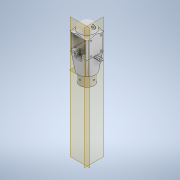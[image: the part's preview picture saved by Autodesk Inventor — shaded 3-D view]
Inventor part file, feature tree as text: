
AUTODESK INVENTOR PART (.ipt)
format: ipt  version: 2022.3 (Build 263350000, 350)  size: 754,688 bytes
history: native  units: mm
features: sketch x23, extrude x15, thicken_offset x6, fillet x5, hole x5, plane x4, revolve x2, mirror x2, projected_geometry x2, loft x1, sweep x1, other x1
ambient origin geometry x8: Origin, YZ Plane, XZ Plane, XY Plane, X Axis, Y Axis, Z Axis, Center Point
bodies: Solid1 (feature_tree)
feature tree (67):
  extrude  "Extrusion1"  Depth=4.0mm
  revolve  "Revolution1"  [1 undecoded]
  plane  "Work Plane1"
  extrude  "Extrusion2"  Depth=100.0mm
  extrude  "Extrusion3"  Depth=150.0mm
  plane  "Work Plane2"
  sketch  "Sketch5"  dims[d12=100.0mm d13=90.0deg]
  fillet  "Fillet1"  Radius=4.0mm
  loft  "Loft1"
  extrude  "Extrusion4"  Depth=5.0mm
  sketch  "Sketch11"  dims[d16=65.0mm d17=65.0mm]
  extrude  "Extrusion7"  Depth=65.0mm
  extrude  "Extrusion8"  Depth=15.0mm
  extrude  "Extrusion9"  Depth=5.0mm TaperAngle=0.0deg
  hole  "Hole2"  [1 undecoded]
  extrude  "Extrusion10"  Depth=50.0mm
  revolve  "Revolution2"  Angle=90.0deg
  fillet  "Fillet3"  [1 undecoded]
  hole  "Hole3"  [1 undecoded]
  hole  "Hole4"  [1 undecoded]
  extrude  "Extrusion14"  Depth=45.0mm
  sketch  "Sketch22"  dims[d58=45.0mm d59=0.0mm d60=45.0mm]
  extrude  "Extrusion15"  Depth=42.0mm TaperAngle=0.0deg
  extrude  "Extrusion16"  Depth=31.0mm
  plane  "Work Plane3"
  plane  "Work Plane4"
  sketch  "Sketch23"  dims[d61=22.0mm d62=42.0mm d63=0.0mm]
  sketch  "Sketch24"  dims[d64=31.0mm d65=31.0mm]
  hole  "Hole5"  [1 undecoded]
  hole  "Hole6"  [1 undecoded]
  mirror  "Mirror1"
  mirror  "Mirror2"
  thicken_offset  "Thicken1"
  thicken_offset  "Thicken2"
  thicken_offset  "Thicken3"
  thicken_offset  "Thicken4"
  thicken_offset  "Thicken5"
  extrude  "Extrusion17"  Depth=10.0mm
  fillet  "Fillet4"  [1 undecoded]
  extrude  "Extrusion18"  Depth=5.0mm
  extrude  "Extrusion19"  Depth=5.068mm
  fillet  "Fillet5"  Radius=5.0mm
  sweep  "Sweep1"
  thicken_offset  "Thicken6"
  extrude  "Extrusion20"  Depth=5.0mm
  fillet  "Fillet6"  Radius=5.068mm
  sketch  "Sketch1"  dims[d0=80.0mm d1=4.0mm]
  sketch  "Sketch2"  dims[d2=40.0mm d3=0.0mm d4=88.0mm]
  sketch  "Sketch3"  dims[d5=50.0mm d8=100.0mm]
  sketch  "Sketch4"  dims[d9=25.0mm d10=150.0mm d11=4.0mm]
  other  "Edges1"
  sketch  "Sketch7"  dims[d14=-52.5mm d15=5.0mm]
  projected_geometry  "Projected Loop2"
  sketch  "Sketch12"  dims[d18=5.0mm d19=15.0mm]
  sketch  "Sketch13"  dims[d20=10.0mm d21=5.0mm d22=0.0mm]
  sketch  "Sketch14"  dims[d23=52.0mm d24=52.0mm]
  sketch  "Sketch15"  dims[d25=5.0mm d26=0.0mm d27=50.0mm]
  sketch  "Sketch16"  dims[d28=5.0mm d29=0.0mm d30=90.0deg d31=0.0mm d32=90.0deg]
  sketch  "Sketch17"  dims[d33=100.0mm d34=0.0mm d54=5.0mm]
  sketch  "Sketch21"  dims[d55=4.5mm d56=5.0mm d57=0.0mm]
  sketch  "Sketch25"  dims[d66=3.4mm d67=6.0mm d68=5.9mm d69=2.0mm d70=90.0deg d71=5.0mm d72=0.0mm d73=3.0mm d74=0.0mm]
  sketch  "Sketch26"  dims[d75=26.0mm d76=26.0mm]
  sketch  "Sketch27"  dims[d77=90.0deg d78=10.0mm d79=0.0mm]
  projected_geometry  "Projected Loop3"
  sketch  "Sketch28"  dims[d80=5.0mm d81=5.0mm]
  sketch  "3D Sketch1"
  sketch  "Sketch29"  dims[d82=5.0mm d83=5.068mm d84=3.4mm d85=6.0mm d86=4.1mm d87=5.1mm d88=90.0deg d89=2.2mm d90=0.0mm d91=5.0mm d92=5.0mm d93=5.0mm d94=5.068mm d95=3.4mm d96=6.0mm d97=4.1mm d98=5.1mm d99=90.0deg d100=2.2mm d101=0.0mm d102=30.0mm d103=40.0mm d104=30.0mm d105=40.0mm d143=10.0mm d144=0.0mm d145=30.0mm d146=10.0mm d147=0.0mm d148=30.0mm d149=0.0mm d150=21.0mm d151=21.0mm d152=3.4mm d153=6.0mm d154=4.1mm d155=5.1mm d156=90.0deg d157=1.2mm d158=0.0mm d159=3.4mm d160=6.0mm d161=4.1mm d162=5.1mm d163=90.0deg d164=1.2mm d165=0.0mm d166=42.0mm d167=0.5mm d168=0.5mm d169=0.5mm d170=0.5mm d171=1.0mm d172=1.0mm d173=1.0mm d174=1.0mm d175=1.0mm d176=1.0mm d177=10.0mm d178=10.0mm d179=12.0mm d180=12.0mm d181=7.0mm d182=2.0mm d183=2.5mm d184=2.5mm d185=0.0mm d186=0.0mm d187=2.0mm d188=17.0mm d189=5.0mm d190=21.0mm d191=5.0mm d192=5.5mm d193=5.5mm d194=0.0mm d195=0.0mm d196=11.0mm d197=7.0mm d198=0.0mm d199=0.0mm d200=2.0mm d201=2.0mm d202=2.0mm d203=0.0mm d204=0.0mm d205=18.0mm d206=30.0mm d207=10.0mm d208=10.0mm d209=15.0mm d210=0.0mm d211=2.0mm d125=0.872665mm d126=0.872665mm d131=1.0mm d132=1.0mm d133=1.0mm d134=0.15mm d135=0.25mm d136=0.375mm d137=14.3117mm d138=0.75mm d139=20.594885mm d140=0.0625mm d141=0.75mm d142=0.375mm]
note: 8 required parameter values undecoded (feature->parameter linkage not recoverable at this tier; creation-order binding heuristic only, values carry confidence <= 0.55)